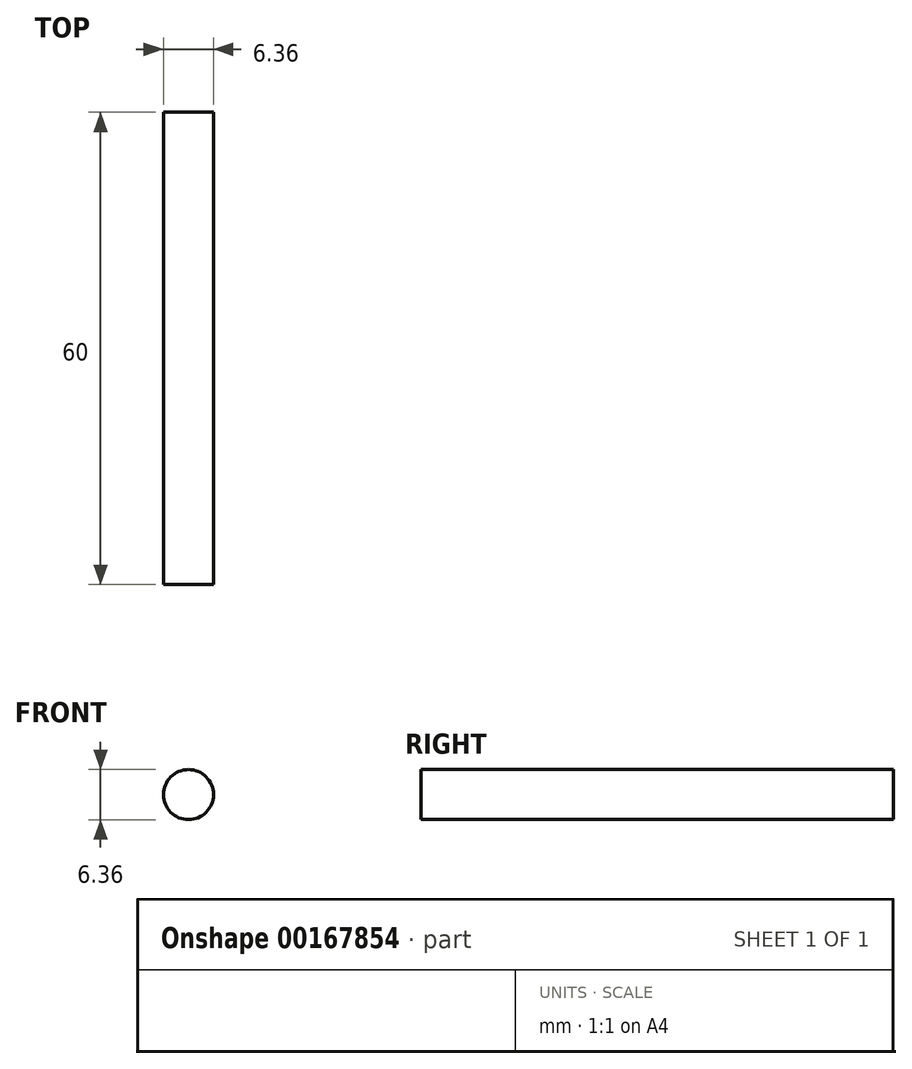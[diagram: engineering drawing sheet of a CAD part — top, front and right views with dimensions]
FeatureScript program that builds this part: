
annotation { "Feature Type Name" : "Feature", "Feature Type Description" : "" }
export const myFeature = defineFeature(function(context is Context, id is Id, definition is map)
    precondition{}
    {
        {
            var Q0;
            Q0=qCreatedBy(makeId("Front.planeOp"),FACE);
            var sketch = newSketch(context, id + "F0", { "sketchPlane" : qUnion([Q0])});
            skCircle(sketch, "E0", {"center": v(0, 0) * mm, "radius": 3.18 * mm});
            skSolve(sketch);
        }
        {
            var Q0;
            Q0 = qSketchRegion(id + "F0", true);
            extrude(context, id + "F1", {"entities" : qUnion([Q0]), "depth" : 60 * mm});
        }
    });
